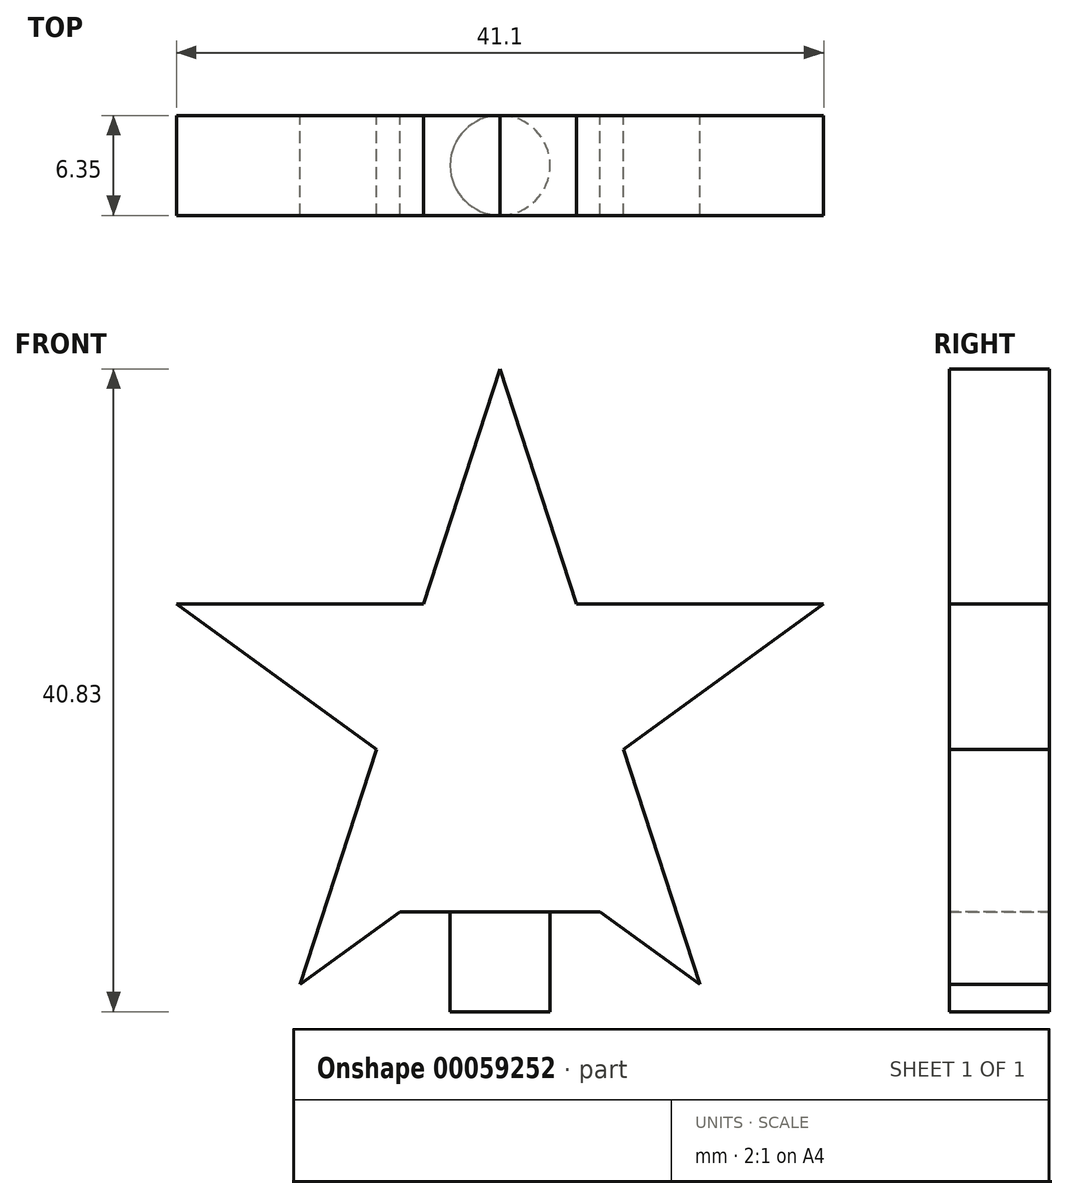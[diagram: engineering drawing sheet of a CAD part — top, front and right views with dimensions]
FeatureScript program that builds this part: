
annotation { "Feature Type Name" : "Feature", "Feature Type Description" : "" }
export const myFeature = defineFeature(function(context is Context, id is Id, definition is map)
    precondition{}
    {
        {
            var Q0;
            Q0=qCreatedBy(makeId("Front.planeOp"),FACE);
            var sketch = newSketch(context, id + "F0", { "sketchPlane" : qUnion([Q0])});
            skCircle(sketch, "E0.cCircle", {"center": v(0, 0) * mm, "radius": 17.48 * mm, "construction": true});
            skLineSegment(sketch, "E0.0", {"start": v(20.55, 6.68) * mm, "end": v(12.7, -17.48) * mm, "construction": true});
            skLineSegment(sketch, "E0.1", {"start": v(12.7, -17.48) * mm, "end": v(-12.7, -17.48) * mm, "construction": true});
            skLineSegment(sketch, "E0.2", {"start": v(-12.7, -17.48) * mm, "end": v(-20.55, 6.68) * mm, "construction": true});
            skLineSegment(sketch, "E0.3", {"start": v(-20.55, 6.68) * mm, "end": v(0, 21.6) * mm, "construction": true});
            skLineSegment(sketch, "E0.4", {"start": v(0, 21.6) * mm, "end": v(20.55, 6.68) * mm, "construction": true});
            skPoint(sketch, "E0.0.midPoint", {"position": v(16.62, -5.4) * mm});
            skLineSegment(sketch, "E1", {"start": v(0, 21.6) * mm, "end": v(-4.85, 6.68) * mm});
            skLineSegment(sketch, "E2", {"start": v(-12.7, -17.48) * mm, "end": v(-6.35, -12.87) * mm});
            skLineSegment(sketch, "E3", {"start": v(-20.55, 6.68) * mm, "end": v(-4.85, 6.68) * mm});
            skLineSegment(sketch, "E4", {"start": v(-20.55, 6.68) * mm, "end": v(-7.85, -2.55) * mm});
            skLineSegment(sketch, "E5", {"start": v(12.7, -17.48) * mm, "end": v(7.85, -2.55) * mm});
            skLineSegment(sketch, "E6.trimOffspring", {"start": v(-7.85, -2.55) * mm, "end": v(-12.7, -17.48) * mm});
            skLineSegment(sketch, "E7.trimOffspring", {"start": v(4.85, 6.68) * mm, "end": v(20.55, 6.68) * mm});
            skLineSegment(sketch, "E8.trimOffspring", {"start": v(6.35, -12.87) * mm, "end": v(12.7, -17.48) * mm});
            skLineSegment(sketch, "E9.trimOffspring", {"start": v(7.85, -2.55) * mm, "end": v(20.55, 6.68) * mm});
            skLineSegment(sketch, "E10.trimOffspring", {"start": v(4.85, 6.68) * mm, "end": v(0, 21.6) * mm});
            skLineSegment(sketch, "E11", {"start": v(-6.35, -12.87) * mm, "end": v(6.35, -12.87) * mm});
            skSolve(sketch);
        }
        {
            var Q0;
            Q0 = qSketchRegion(id + "F0", true);
            extrude(context, id + "F1", {"entities" : qUnion([Q0]), "depth" : 6.35 * mm});
        }
        {
            var Q0;
            Q0=makeQuery(id+"F1.opExtrude","SWEPT_FACE",FACE,{"disambiguationData":[OSD([sQuery(id+"F0.wireOp",EDGE,"E11")])]});
            var sketch = newSketch(context, id + "F2", { "sketchPlane" : qUnion([Q0])});
            skCircle(sketch, "E12", {"center": v(0, 3.18) * mm, "radius": 3.18 * mm});
            skPoint(sketch, "E12.centerSnap0", {"position": v(6.35, 3.18) * mm});
            skSolve(sketch);
        }
        {
            var Q0;
            Q0 = qSketchRegion(id + "F2", true);
            extrude(context, id + "F3", {"entities" : qUnion([Q0]), "operationType" : NewBodyOperationType.ADD, "depth" : 6.35 * mm});
        }
    });
